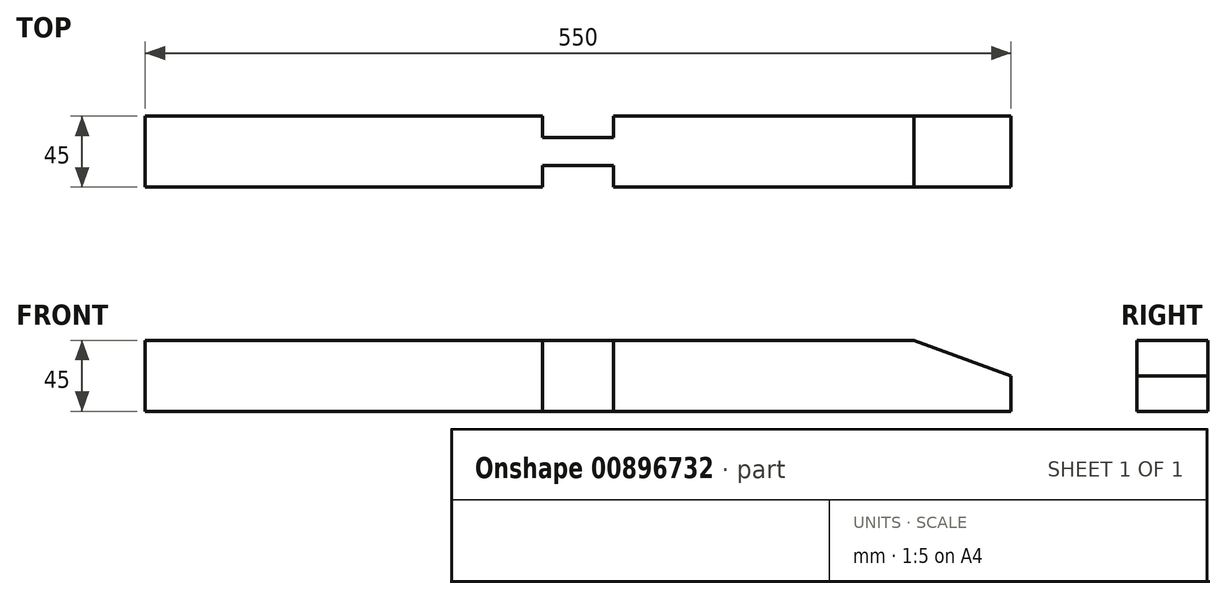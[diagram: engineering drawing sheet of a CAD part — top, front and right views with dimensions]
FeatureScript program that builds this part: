
annotation { "Feature Type Name" : "Feature", "Feature Type Description" : "" }
export const myFeature = defineFeature(function(context is Context, id is Id, definition is map)
    precondition{}
    {
        {
            var Q0;
            Q0=qCreatedBy(makeId("Right.planeOp"),FACE);
            var sketch = newSketch(context, id + "F0", { "sketchPlane" : qUnion([Q0])});
            skLineSegment(sketch, "E0.bottom", {"start": v(22.5, 22.5) * mm, "end": v(-22.5, 22.5) * mm});
            skLineSegment(sketch, "E0.top", {"start": v(22.5, -22.5) * mm, "end": v(-22.5, -22.5) * mm});
            skLineSegment(sketch, "E0.left", {"start": v(22.5, 22.5) * mm, "end": v(22.5, -22.5) * mm});
            skLineSegment(sketch, "E0.right", {"start": v(-22.5, 22.5) * mm, "end": v(-22.5, -22.5) * mm});
            skPoint(sketch, "E0.middle", {"position": v(0, 0) * mm});
            skSolve(sketch);
        }
        {
            var Q0;
            Q0 = qSketchRegion(id + "F0", true);
            extrude(context, id + "F1", {"entities" : qUnion([Q0]), "endBound" : BoundingType.SYMMETRIC, "depth" : 550 * mm, "offsetDistance" : 25 * mm});
        }
        {
            var Q0;
            Q0=makeQuery(id+"F1.opExtrude","SWEPT_FACE",FACE,{"disambiguationData":[OSD([sQuery(id+"F0.wireOp",EDGE,"E0.bottom")])]});
            var sketch = newSketch(context, id + "F2", { "sketchPlane" : qUnion([Q0])});
            skLineSegment(sketch, "E1.bottom", {"start": v(-22.5, 22.5) * mm, "end": v(22.5, 22.5) * mm});
            skLineSegment(sketch, "E1.top", {"start": v(-22.5, 9) * mm, "end": v(22.5, 9) * mm});
            skLineSegment(sketch, "E1.left", {"start": v(-22.5, 22.5) * mm, "end": v(-22.5, 9) * mm});
            skLineSegment(sketch, "E1.right", {"start": v(22.5, 22.5) * mm, "end": v(22.5, 9) * mm});
            skLineSegment(sketch, "E2.bottom", {"start": v(-22.5, -22.5) * mm, "end": v(22.5, -22.5) * mm});
            skLineSegment(sketch, "E2.top", {"start": v(-22.5, -9) * mm, "end": v(22.5, -9) * mm});
            skLineSegment(sketch, "E2.left", {"start": v(-22.5, -22.5) * mm, "end": v(-22.5, -9) * mm});
            skLineSegment(sketch, "E2.right", {"start": v(22.5, -22.5) * mm, "end": v(22.5, -9) * mm});
            skLineSegment(sketch, "E3", {"start": v(-35.38, 0) * mm, "end": v(36.75, 0) * mm, "construction": true});
            skLineSegment(sketch, "E4", {"start": v(0, -32.8) * mm, "end": v(0, 36.21) * mm, "construction": true});
            skSolve(sketch);
        }
        {
            var Q0;
            Q0 = qSketchRegion(id + "F2", true);
            extrude(context, id + "F3", {"entities" : qUnion([Q0]), "operationType" : NewBodyOperationType.REMOVE, "endBound" : BoundingType.THROUGH_ALL, "oppositeDirection" : true, "depth" : 25 * mm, "offsetDistance" : 25 * mm});
        }
        {
            var Q0;
            {var subQ1=sQuery(id+"F0.wireOp",EDGE,"E0.right");Q0=makeQuery(id+"F3.boolean.opBoolean","SPLIT",FACE,{"disambiguationData":[TD([makeQuery(id+"F3.opExtrude","SWEPT_FACE",FACE,{"disambiguationData":[OSD([sQuery(id+"F2.wireOp",EDGE,"E2.right")])]})])],"derivedFrom":makeQuery(id+"F1.opExtrude","SWEPT_FACE",FACE,{"disambiguationData":[OSD([subQ1])]})});}
            var sketch = newSketch(context, id + "F4", { "sketchPlane" : qUnion([Q0])});
            skLineSegment(sketch, "E5", {"start": v(213.18, 22.5) * mm, "end": v(275, 0) * mm});
            skLineSegment(sketch, "E6", {"start": v(275, 0) * mm, "end": v(275, 22.5) * mm});
            skLineSegment(sketch, "E7", {"start": v(275, 22.5) * mm, "end": v(213.18, 22.5) * mm});
            skSolve(sketch);
        }
        {
            var Q0;
            Q0=makeQuery(id+"F4.imprint","IMPRINT",FACE,{"disambiguationData":[TD([[makeQuery(id+"F4.imprint","IMPRINT",EDGE,{"derivedFrom":sQuery(id+"F4.wireOp",EDGE,"E5")}),1.0]])]});
            extrude(context, id + "F5", {"entities" : qUnion([Q0]), "operationType" : NewBodyOperationType.REMOVE, "endBound" : BoundingType.THROUGH_ALL, "oppositeDirection" : true, "depth" : 25 * mm, "offsetDistance" : 25 * mm});
        }
    });
